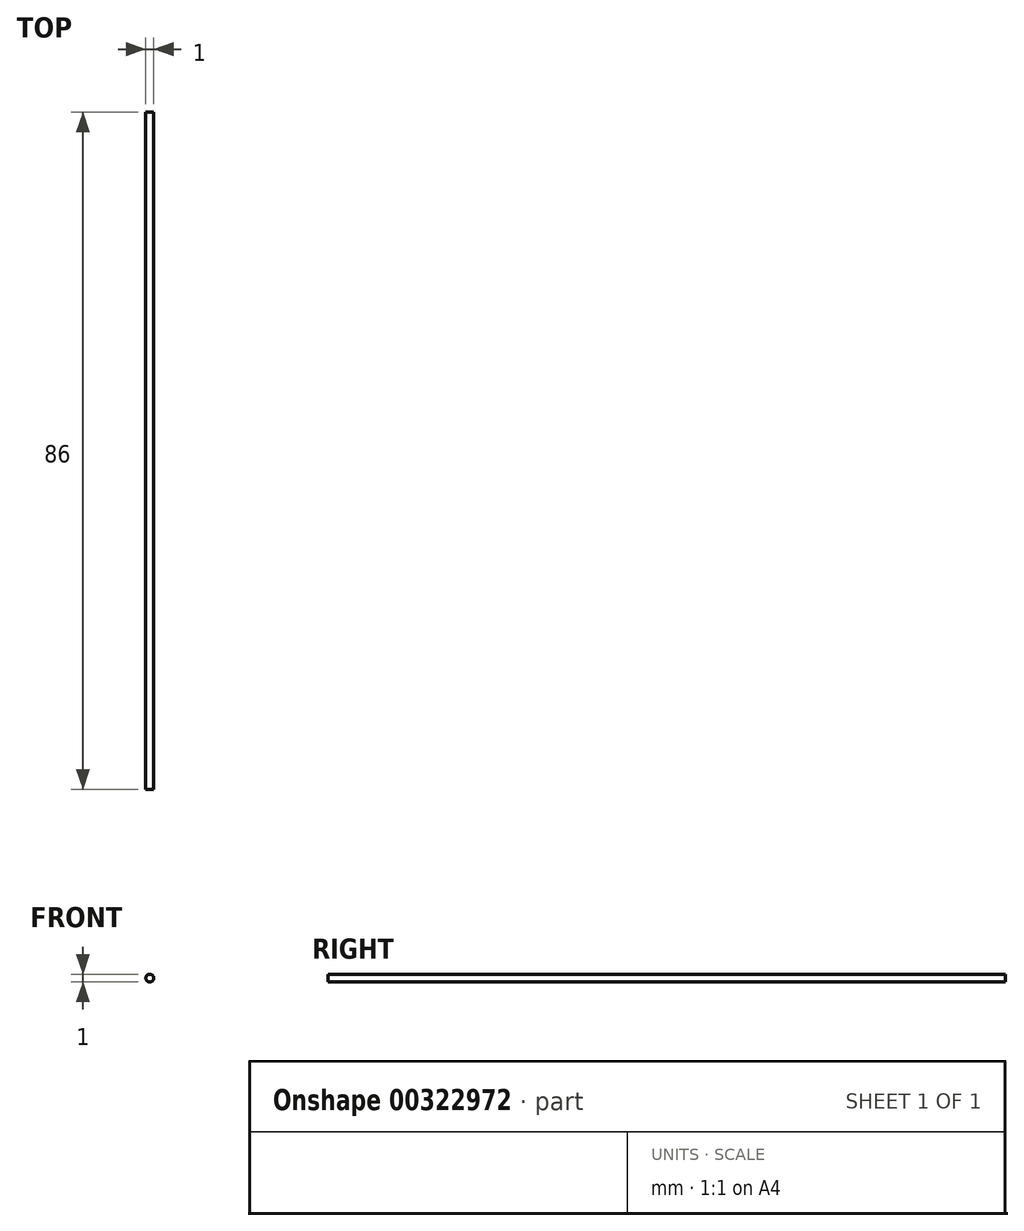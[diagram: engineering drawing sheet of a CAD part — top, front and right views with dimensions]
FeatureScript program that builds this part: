
annotation { "Feature Type Name" : "Feature", "Feature Type Description" : "" }
export const myFeature = defineFeature(function(context is Context, id is Id, definition is map)
    precondition{}
    {
        {
            var Q0;
            Q0=qCreatedBy(makeId("Front.planeOp"),FACE);
            var sketch = newSketch(context, id + "F0", { "sketchPlane" : qUnion([Q0])});
            skCircle(sketch, "E0", {"center": v(0, 0) * mm, "radius": 0.5 * mm});
            skSolve(sketch);
        }
        {
            var Q0;
            Q0 = qSketchRegion(id + "F0", true);
            extrude(context, id + "F1", {"entities" : qUnion([Q0]), "depth" : 86 * mm});
        }
    });
